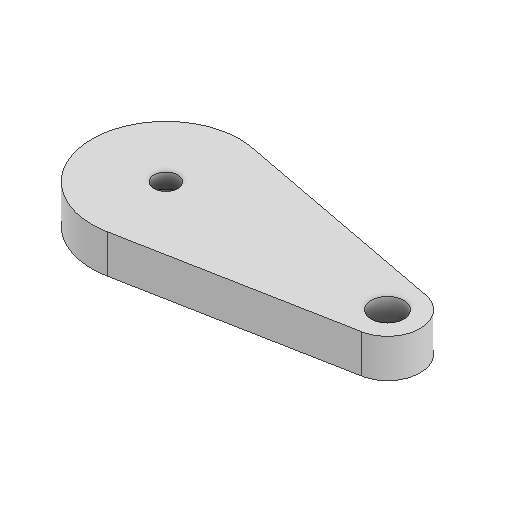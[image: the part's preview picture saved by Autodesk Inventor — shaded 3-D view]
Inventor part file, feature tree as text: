
AUTODESK INVENTOR PART (.ipt)
format: ipt  version: 2025.1 (Build 291241020, 241B)  size: 137,216 bytes
history: native  units: in
note: dims shown in document units (in); Inventor stores cm internally (conversion verified against a paired STEP export)
features: sketch x3, extrude x2, projected_geometry x1
ambient origin geometry x8: Origin, YZ Plane, XZ Plane, XY Plane, X Axis, Y Axis, Z Axis, Center Point
bodies: Solid1 (feature_tree)
feature tree (6):
  extrude  "Extrusion1"  Depth=0.5in
  extrude  "Extrusion2"  Depth=0.75in
  sketch  "Sketch1"  dims[d0=0.184in d1=0.5in]
  sketch  "Sketch2"  dims[d4=0.11in d5=0.08in d6=0.0in d7=0.08in d8=0.05in d9=0.0in d10=0.01in d11=11.811in d13=360.0deg]
  projected_geometry  "Projected Loop1"
  sketch  "Sketch Circular Pattern1"  dims[d2=0.75in d3=0.22in]
